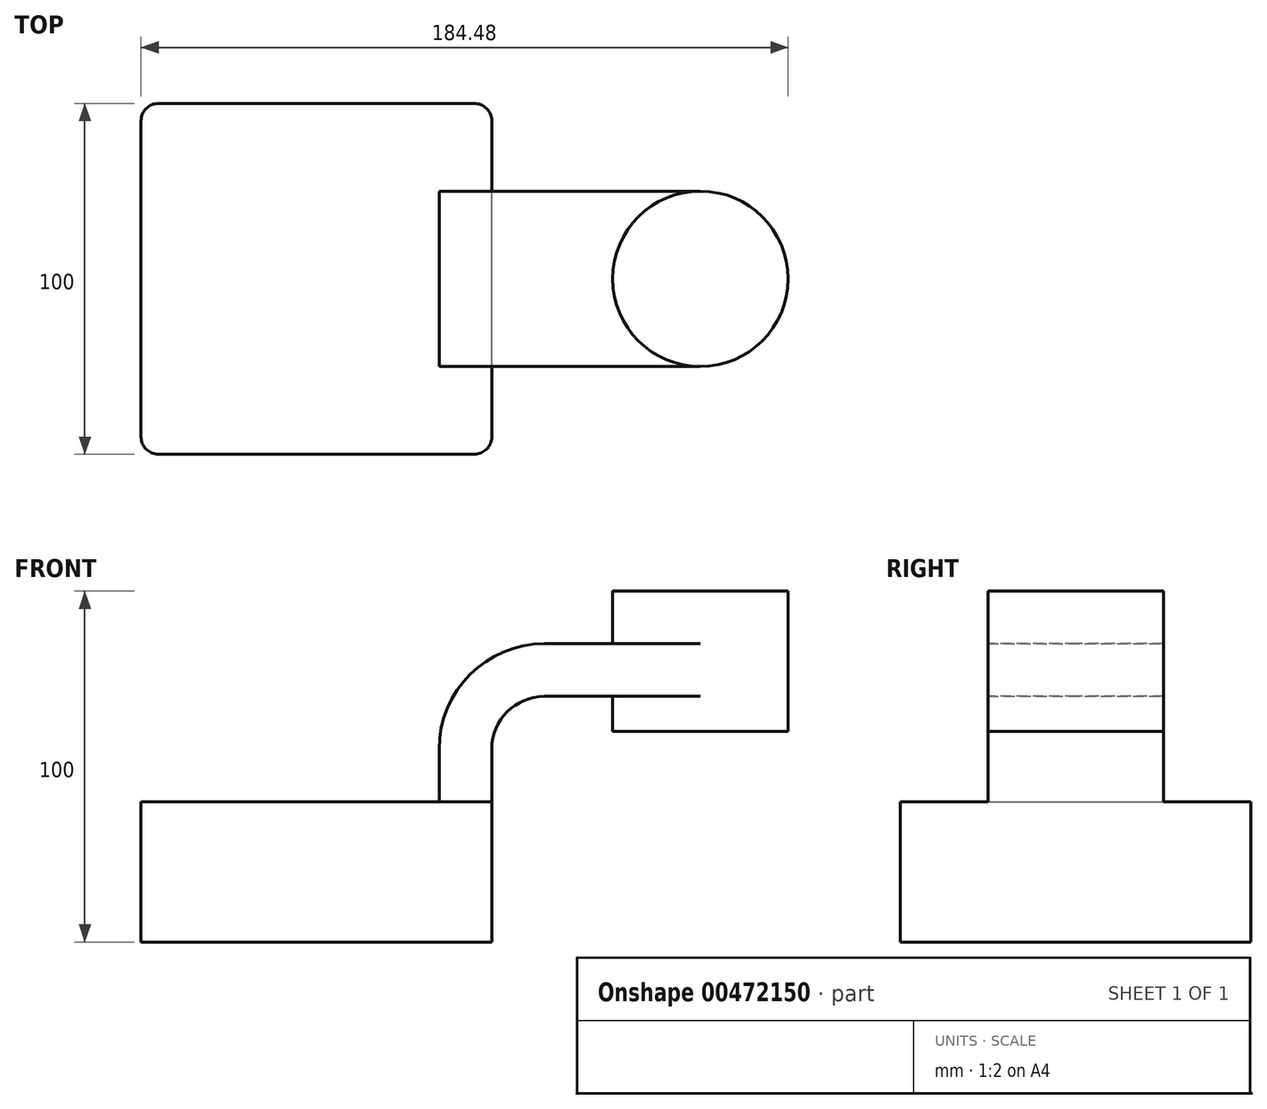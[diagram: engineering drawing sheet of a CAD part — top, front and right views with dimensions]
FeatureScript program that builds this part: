
annotation { "Feature Type Name" : "Feature", "Feature Type Description" : "" }
export const myFeature = defineFeature(function(context is Context, id is Id, definition is map)
    precondition{}
    {
        {
            var Q0;
            Q0=qCreatedBy(makeId("Front.planeOp"),FACE);
            var sketch = newSketch(context, id + "F0", { "sketchPlane" : qUnion([Q0])});
            skLineSegment(sketch, "E0.bottom", {"start": v(-50, 20) * mm, "end": v(50, 20) * mm});
            skLineSegment(sketch, "E0.top", {"start": v(-50, -20) * mm, "end": v(50, -20) * mm});
            skLineSegment(sketch, "E0.left", {"start": v(-50, 20) * mm, "end": v(-50, -20) * mm});
            skLineSegment(sketch, "E0.right", {"start": v(50, 20) * mm, "end": v(50, -20) * mm});
            skPoint(sketch, "E0.middle", {"position": v(0, 0) * mm});
            skLineSegment(sketch, "E1.bottom", {"start": v(84.48, 80) * mm, "end": v(134.48, 80) * mm});
            skLineSegment(sketch, "E1.top", {"start": v(84.48, 40) * mm, "end": v(134.48, 40) * mm});
            skLineSegment(sketch, "E1.left", {"start": v(84.48, 80) * mm, "end": v(84.48, 40) * mm});
            skLineSegment(sketch, "E1.right", {"start": v(134.48, 80) * mm, "end": v(134.48, 40) * mm});
            skPoint(sketch, "E1.middle", {"position": v(109.48, 60) * mm});
            skLineSegment(sketch, "E2", {"start": v(50, 20) * mm, "end": v(50, 35) * mm});
            skArc(sketch, "E3", {"start": v(50, 35) * mm, "mid": v(54.4, 45.6) * mm, "end": v(65, 50) * mm});
            skLineSegment(sketch, "E4", {"start": v(65, 50) * mm, "end": v(109.48, 50) * mm});
            skLineSegment(sketch, "E5.0", {"start": v(65, 65) * mm, "end": v(109.48, 65) * mm});
            skArc(sketch, "E5.1", {"start": v(35, 35) * mm, "mid": v(43.79, 56.21) * mm, "end": v(65, 65) * mm});
            skLineSegment(sketch, "E5.2", {"start": v(35, 20) * mm, "end": v(35, 35) * mm});
            skFitSpline(sketch, "E6", {"points": [v(-50, 20) * mm, v(65, 65) * mm], "startDerivative": vector(55.93, 138.01) * mm, "endDerivative": vector(195, -0.56) * mm});
            skLineSegment(sketch, "E7", {"start": v(109.48, 40) * mm, "end": v(109.48, 80) * mm});
            skSolve(sketch);
        }
        {
            var Q0;
            Q0=makeQuery(id+"F0.imprint","IMPRINT",FACE,{"disambiguationData":[TD([[makeQuery(id+"F0.imprint","IMPRINT",EDGE,{"derivedFrom":sQuery(id+"F0.wireOp",EDGE,"E0.top")}),1.0]])]});
            extrude(context, id + "F1", {"entities" : qUnion([Q0]), "endBound" : BoundingType.SYMMETRIC, "depth" : 100 * mm});
        }
        {
            var Q0;
            {var subQ1=sQuery(id+"F0.wireOp",EDGE,"E2");Q0=makeQuery(id+"F0.imprint","IMPRINT",FACE,{"disambiguationData":[TD([[makeQuery(id+"F0.imprint","IMPRINT",EDGE,{"derivedFrom":subQ1}),1.0]])]});}
            var Q1;
            {var subQ0=sQuery(id+"F0.wireOp",EDGE,"E5.0");var subQ1=sQuery(id+"F0.wireOp",EDGE,"E1.left");var subQ2=makeQuery(id+"F0.imprint","INTERSECT",VERTEX,{"derivedFrom":[subQ1,subQ0]});Q1=makeQuery(id+"F0.imprint","IMPRINT",FACE,{"disambiguationData":[TD([[makeQuery(id+"F0.imprint","IMPRINT",EDGE,{"disambiguationData":[TD([[subQ2,-1.0]])],"derivedFrom":subQ1}),1.0]])]});}
            extrude(context, id + "F2", {"entities" : qUnion([Q0, Q1]), "operationType" : NewBodyOperationType.ADD, "endBound" : BoundingType.SYMMETRIC, "depth" : 50 * mm});
        }
        {
            var Q0;
            Q0=makeQuery(id+"F0.imprint","IMPRINT",FACE,{"disambiguationData":[TD([[makeQuery(id+"F0.imprint","IMPRINT",EDGE,{"derivedFrom":sQuery(id+"F0.wireOp",EDGE,"E5.1")}),1.0]])]});
            extrude(context, id + "F3", {"entities" : qUnion([Q0]), "operationType" : NewBodyOperationType.ADD, "endBound" : BoundingType.SYMMETRIC, "depth" : 25 * mm});
        }
        {
            var Q0;
            {var subQ4=sQuery(id+"F0.wireOp",EDGE,"E1.right");Q0=makeQuery(id+"F0.imprint","IMPRINT",FACE,{"disambiguationData":[TD([[makeQuery(id+"F0.imprint","IMPRINT",EDGE,{"derivedFrom":subQ4}),-1.0]])]});}
            var Q1;
            Q1=sQuery(id+"F0.wireOp",EDGE,"E7");
            revolve(context, id + "F4", {"operationType" : NewBodyOperationType.ADD, "entities" : qUnion([Q0]), "axis" : qUnion([Q1]), "revolveType" : RevolveType.FULL});
        }
        {
            var Q0;
            Q0=makeQuery(id+"F1.opExtrude","CAP_EDGE",EDGE,{"disambiguationData":[OSD([sQuery(id+"F0.wireOp",EDGE,"E0.left")])],"isStart":false});
            var Q1;
            Q1=makeQuery(id+"F1.opExtrude","CAP_EDGE",EDGE,{"disambiguationData":[OSD([sQuery(id+"F0.wireOp",EDGE,"E0.right")])],"isStart":false});
            var Q2;
            Q2=makeQuery(id+"F1.opExtrude","CAP_EDGE",EDGE,{"disambiguationData":[OSD([sQuery(id+"F0.wireOp",EDGE,"E0.left")])],"isStart":true});
            var Q3;
            Q3=makeQuery(id+"F1.opExtrude","CAP_EDGE",EDGE,{"disambiguationData":[OSD([sQuery(id+"F0.wireOp",EDGE,"E0.right")])],"isStart":true});
            fillet(context, id + "F5", {"entities" : qUnion([Q0, Q1, Q2, Q3]), "radius" : 5 * mm, "tangentPropagation" : true, "allowEdgeOverflow" : false});
        }
    });
